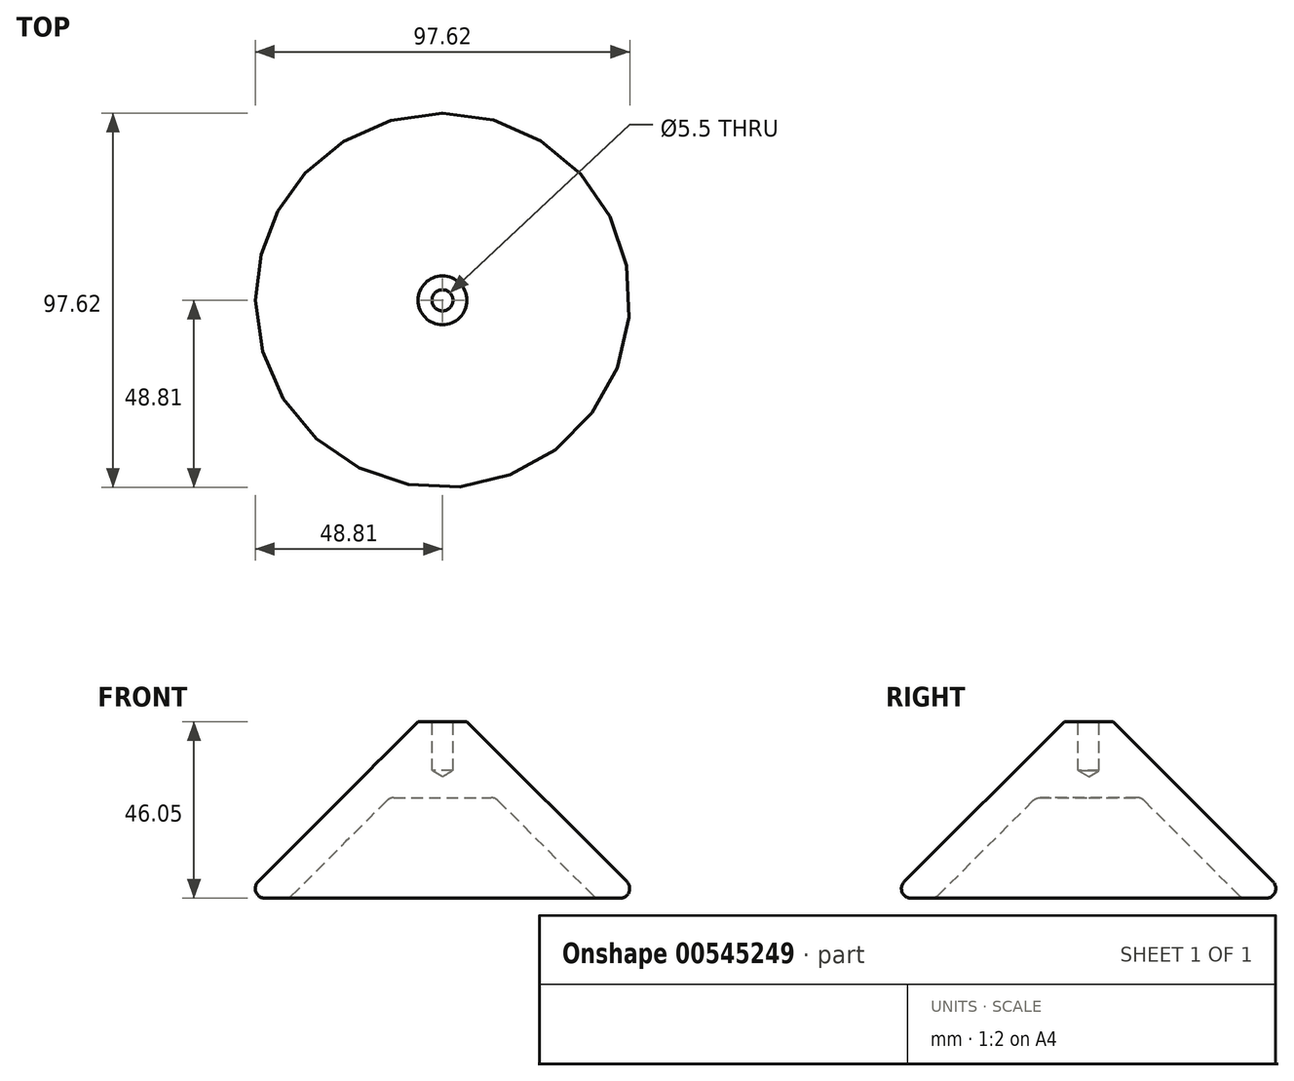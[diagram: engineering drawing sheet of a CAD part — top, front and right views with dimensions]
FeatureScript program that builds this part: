
annotation { "Feature Type Name" : "Feature", "Feature Type Description" : "" }
export const myFeature = defineFeature(function(context is Context, id is Id, definition is map)
    precondition{}
    {
        {
            var Q0;
            Q0=qCreatedBy(makeId("Front.planeOp"),FACE);
            var sketch = newSketch(context, id + "F0", { "sketchPlane" : qUnion([Q0])});
            skLineSegment(sketch, "E0", {"start": v(0, 26.2) * mm, "end": v(0, 46.05) * mm});
            skLineSegment(sketch, "E1", {"start": v(6.35, 46.05) * mm, "end": v(48.06, 4.34) * mm});
            skLineSegment(sketch, "E2", {"start": v(46.27, 0) * mm, "end": v(41, 0) * mm});
            skLineSegment(sketch, "E3", {"start": v(0, 26.2) * mm, "end": v(12.7, 26.2) * mm});
            skPoint(sketch, "E3.endSnap0", {"position": v(0, 26.2) * mm});
            skLineSegment(sketch, "E4", {"start": v(14.5, 25.46) * mm, "end": v(39.2, 0.74) * mm});
            skPoint(sketch, "E5.orphan", {"position": v(0, 0) * mm});
            skPoint(sketch, "E6.visualSharp", {"position": v(13.75, 26.2) * mm});
            skArc(sketch, "E6.filletArc", {"start": v(14.5, 25.46) * mm, "mid": v(13.67, 26) * mm, "end": v(12.7, 26.2) * mm});
            skPoint(sketch, "E7.visualSharp", {"position": v(39.95, 0) * mm});
            skArc(sketch, "E7.filletArc", {"start": v(39.2, 0.74) * mm, "mid": v(40.03, 0.2) * mm, "end": v(41, 0) * mm});
            skLineSegment(sketch, "E8", {"start": v(0, 46.05) * mm, "end": v(6.35, 46.05) * mm});
            skPoint(sketch, "E9.orphan", {"position": v(0, 52.4) * mm});
            skPoint(sketch, "E10.visualSharp", {"position": v(52.4, 0) * mm});
            skArc(sketch, "E10.filletArc", {"start": v(46.27, 0) * mm, "mid": v(48.61, 1.57) * mm, "end": v(48.06, 4.34) * mm});
            skSolve(sketch);
        }
        {
            var Q0;
            Q0 = qSketchRegion(id + "F0", true);
            var Q1;
            Q1=sQuery(id+"F0.wireOp",EDGE,"E0");
            revolve(context, id + "F1", {"entities" : qUnion([Q0]), "axis" : qUnion([Q1]), "revolveType" : RevolveType.FULL});
        }
        {
            var Q0;
            Q0=makeQuery(id+"F1.opRevolve","SWEPT_FACE",FACE,{"disambiguationData":[OSD([sQuery(id+"F0.wireOp",EDGE,"E8")])]});
            var sketch = newSketch(context, id + "F2", { "sketchPlane" : qUnion([Q0])});
            skPoint(sketch, "E11", {"position": v(0, 0) * mm});
            skSolve(sketch);
        }
        {
            var Q0;
            Q0=sQuery(id+"F2.wireOp",VERTEX,"E11");
            var Q1;
            Q1=makeQuery(id+"F1.opRevolve","SWEPT_BODY",BODY,{"disambiguationData":[OSD([sQuery(id+"F0.wireOp",EDGE,"E0"),sQuery(id+"F0.wireOp",EDGE,"E1"),sQuery(id+"F0.wireOp",EDGE,"E2"),sQuery(id+"F0.wireOp",EDGE,"E3"),sQuery(id+"F0.wireOp",EDGE,"E4"),sQuery(id+"F0.wireOp",EDGE,"E6.filletArc"),sQuery(id+"F0.wireOp",EDGE,"E7.filletArc"),sQuery(id+"F0.wireOp",EDGE,"E8"),sQuery(id+"F0.wireOp",EDGE,"E10.filletArc")])]});
            hole(context, id + "F3", {"style" : HoleStyle.SIMPLE, "endStyle" : HoleEndStyle.BLIND, "standardTappedOrClearance" : lookupTablePath({ "standard" : "ISO", "fit" : "Normal", "size" : "M5", "type" : "Clearance" }), "standardBlindInLast" : lookupTablePath({ "fit" : "Standard", "standard" : "ISO", "size" : "M5", "type" : "Clearance" }), "holeDiameter" : 5.5 * mm, "holeDepth" : 12.7 * mm, "isTappedThrough" : true, "tappedDepth" : 12.7 * mm, "tapClearance" : 3, "startFromSketch" : true, "locations" : qUnion([Q0]), "scope" : qUnion([Q1])});
        }
    });
